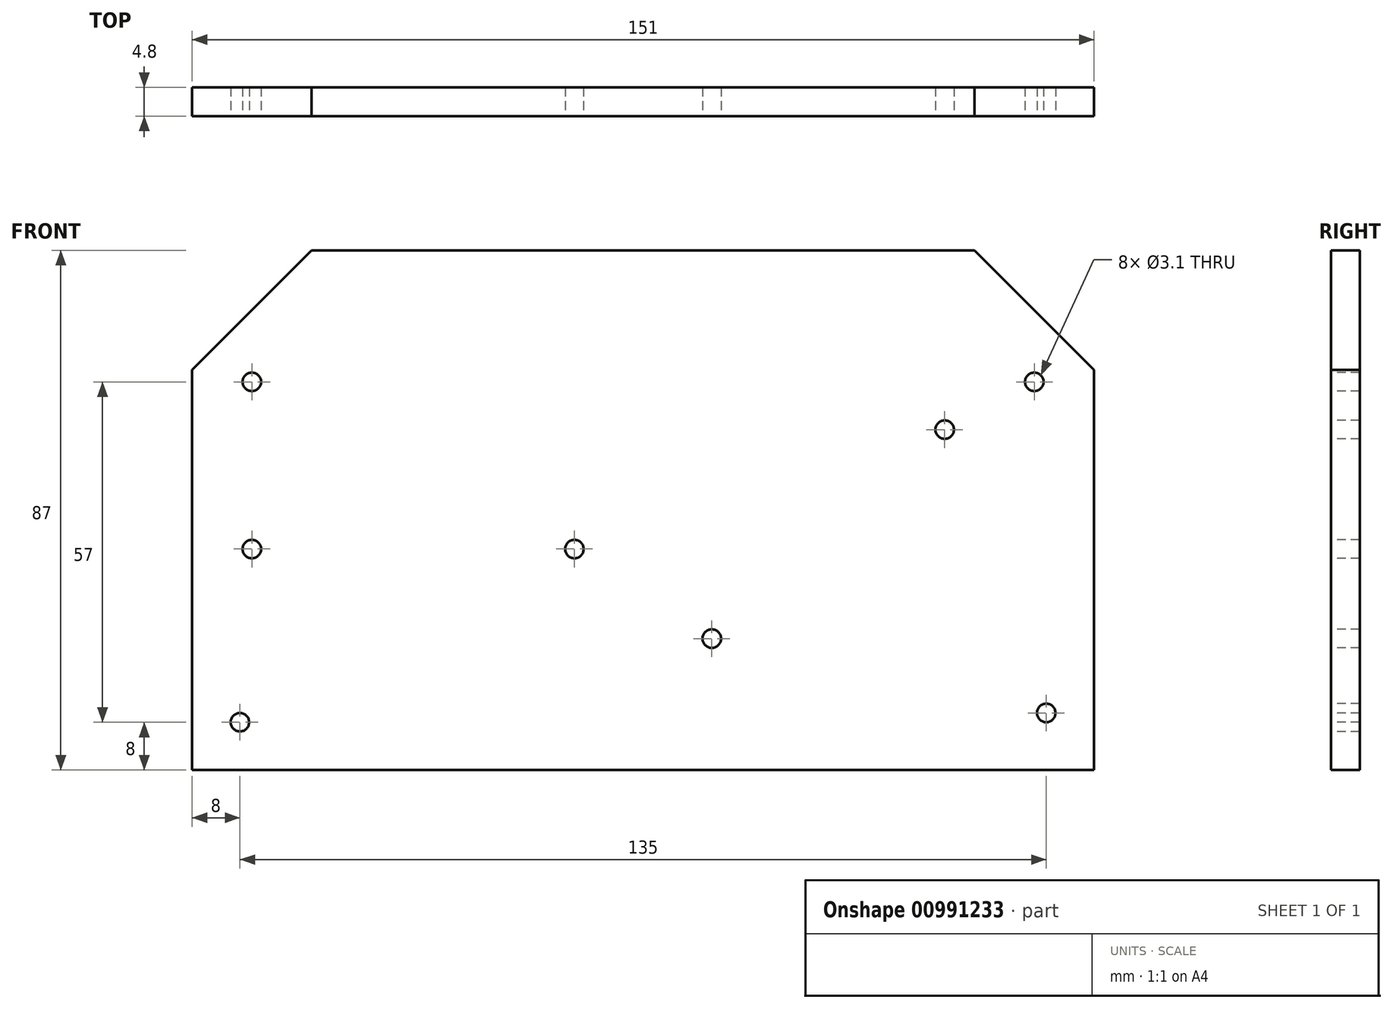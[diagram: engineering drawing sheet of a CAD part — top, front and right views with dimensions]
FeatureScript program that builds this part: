
annotation { "Feature Type Name" : "Feature", "Feature Type Description" : "" }
export const myFeature = defineFeature(function(context is Context, id is Id, definition is map)
    precondition{}
    {
        {
            var Q0;
            Q0=qCreatedBy(makeId("Front.planeOp"),FACE);
            var sketch = newSketch(context, id + "F0", { "sketchPlane" : qUnion([Q0])});
            skLineSegment(sketch, "E0.bottom", {"start": v(75.5, -43.5) * mm, "end": v(-75.5, -43.5) * mm});
            skLineSegment(sketch, "E0.top", {"start": v(75.5, 43.5) * mm, "end": v(-75.5, 43.5) * mm});
            skLineSegment(sketch, "E0.left", {"start": v(75.5, -43.5) * mm, "end": v(75.5, 43.5) * mm});
            skLineSegment(sketch, "E0.right", {"start": v(-75.5, -43.5) * mm, "end": v(-75.5, 43.5) * mm});
            skPoint(sketch, "E0.middle", {"position": v(0, 0) * mm});
            skSolve(sketch);
        }
        {
            var Q0;
            Q0=makeQuery(id+"F0.imprint","IMPRINT",FACE,{"disambiguationData":[TD([[makeQuery(id+"F0.imprint","IMPRINT",EDGE,{"derivedFrom":sQuery(id+"F0.wireOp",EDGE,"E0.bottom")}),-1.0]])]});
            extrude(context, id + "F1", {"entities" : qUnion([Q0]), "depth" : 4.8 * mm, "offsetDistance" : 25 * mm});
        }
        {
            var Q0;
            Q0=makeQuery(id+"F1.opExtrude","CAP_FACE",FACE,{"disambiguationData":[OSD([sQuery(id+"F0.wireOp",EDGE,"E0.bottom"),sQuery(id+"F0.wireOp",EDGE,"E0.top"),sQuery(id+"F0.wireOp",EDGE,"E0.left"),sQuery(id+"F0.wireOp",EDGE,"E0.right")])],"isStart":false});
            var sketch = newSketch(context, id + "F2", { "sketchPlane" : qUnion([Q0])});
            skCircle(sketch, "E1", {"center": v(-65.5, 21.5) * mm, "radius": 1.55 * mm});
            skCircle(sketch, "E2", {"center": v(65.5, 21.5) * mm, "radius": 1.55 * mm});
            skCircle(sketch, "E3", {"center": v(-67.5, -35.5) * mm, "radius": 1.55 * mm});
            skCircle(sketch, "E4", {"center": v(67.5, -33.95) * mm, "radius": 1.55 * mm});
            skCircle(sketch, "E5", {"center": v(50.5, 13.5) * mm, "radius": 1.55 * mm});
            skCircle(sketch, "E6", {"center": v(11.5, -21.5) * mm, "radius": 1.55 * mm});
            skCircle(sketch, "E7", {"center": v(-65.5, -6.5) * mm, "radius": 1.55 * mm});
            skCircle(sketch, "E8", {"center": v(-11.5, -6.5) * mm, "radius": 1.55 * mm});
            skSolve(sketch);
        }
        {
            var Q0;
            Q0=makeQuery(id+"F2.imprint","IMPRINT",FACE,{"disambiguationData":[TD([[makeQuery(id+"F2.imprint","IMPRINT",EDGE,{"derivedFrom":sQuery(id+"F2.wireOp",EDGE,"E7")}),1.0]])]});
            extrude(context, id + "F3", {"entities" : qUnion([Q0]), "operationType" : NewBodyOperationType.REMOVE, "oppositeDirection" : true, "depth" : 4.8 * mm, "offsetDistance" : 25 * mm});
        }
        {
            var Q0;
            Q0 = qSketchRegion(id + "F2", true);
            extrude(context, id + "F4", {"entities" : qUnion([Q0]), "operationType" : NewBodyOperationType.REMOVE, "oppositeDirection" : true, "depth" : 4.8 * mm, "offsetDistance" : 25 * mm});
        }
        {
            var Q0;
            Q0=makeQuery(id+"F1.opExtrude","SWEPT_EDGE",EDGE,{"disambiguationData":[OSD([sQuery(id+"F0.wireOp",EDGE,"E0.top"),sQuery(id+"F0.wireOp",EDGE,"E0.right")])]});
            chamfer(context, id + "F5", {"entities" : qUnion([Q0]), "width" : 20 * mm, "tangentPropagation" : true});
        }
        {
            var Q0;
            Q0=makeQuery(id+"F1.opExtrude","SWEPT_EDGE",EDGE,{"disambiguationData":[OSD([sQuery(id+"F0.wireOp",EDGE,"E0.top"),sQuery(id+"F0.wireOp",EDGE,"E0.left")])]});
            chamfer(context, id + "F6", {"entities" : qUnion([Q0]), "width" : 20 * mm, "tangentPropagation" : true});
        }
    });
